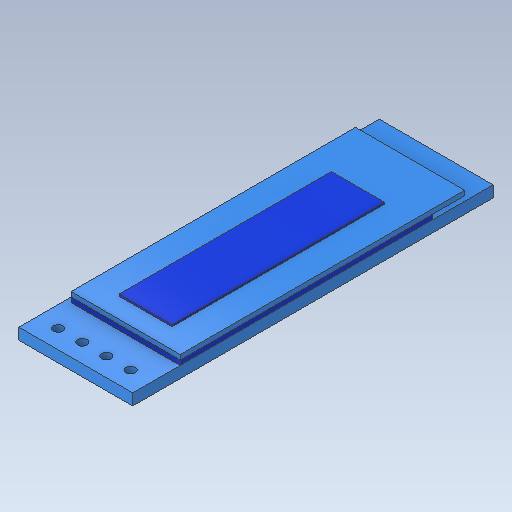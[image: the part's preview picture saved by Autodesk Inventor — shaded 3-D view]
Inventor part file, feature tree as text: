
AUTODESK INVENTOR PART (.ipt)
format: ipt  version: 2020.1 (Build 241239000, 239)  size: 265,728 bytes
history: native  units: mm
features: extrude x7, sketch x5, fillet x1, plane x1
ambient origin geometry x8: Origin, YZ Plane, XZ Plane, XY Plane, X Axis, Y Axis, Z Axis, Center Point
bodies: Solid1 (feature_tree), Solid2 (feature_tree)
feature tree (14):
  sketch  "Sketch1"  dims[d0=12.0mm d1=38.0mm]
  extrude  "Extrusion1"  Depth=38.0mm
  extrude  "Extrusion2"  Depth=30.0mm
  sketch  "Sketch2"  dims[d2=3.0mm d3=30.0mm]
  extrude  "Extrusion3"  Depth=7.58mm
  extrude  "Extrusion4"  Depth=5.58mm
  extrude  "Extrusion5"  Depth=1.96mm
  fillet  "Fillet1"  Radius=7.51mm
  extrude  "Extrusion6"  Depth=2.4mm
  plane  "Work Plane2"
  extrude  "Extrusion7"  Depth=1.96mm
  sketch  "Sketch3"  dims[d5=26.6mm d6=7.58mm]
  sketch  "Sketch4"  dims[d7=24.38mm d8=5.58mm]
  sketch  "Sketch5"  dims[d9=22.38mm d10=1.96mm d11=7.51mm d13=2.19mm d14=1.96mm d15=1.0mm d16=40.0mm d18=2.54mm d19=10.0mm d21=10.0mm d23=1.2mm d24=0.0mm d25=0.5mm d26=0.0mm d27=1.0mm d28=1.2mm d29=0.5mm d30=0.0mm d32=0.001mm d33=0.001mm d34=0.001mm d35=11.5mm d36=0.001mm d37=0.2mm d38=0.0mm d39=0.5mm d40=0.0mm d41=1.0mm d43=2.05mm d46=1.89mm d47=0.282843mm d48=45.0deg d49=0.6mm d50=0.6mm d51=2.4mm d52=0.0mm d53=135.0deg d54=135.0deg d55=135.0deg d56=2.05mm d57=1.89mm d58=0.282843mm d59=45.0deg d60=0.6mm d61=0.6mm d62=135.0deg d63=135.0deg d64=135.0deg d65=2.05mm d66=1.89mm d67=0.282843mm d68=45.0deg d69=0.6mm d70=0.6mm d71=135.0deg d72=135.0deg d73=135.0deg d74=2.05mm d75=1.89mm d76=0.282843mm d77=45.0deg d78=0.6mm d79=0.6mm d80=135.0deg d81=135.0deg d82=135.0deg d85=11.0mm d86=0.0mm d87=1.4mm]
